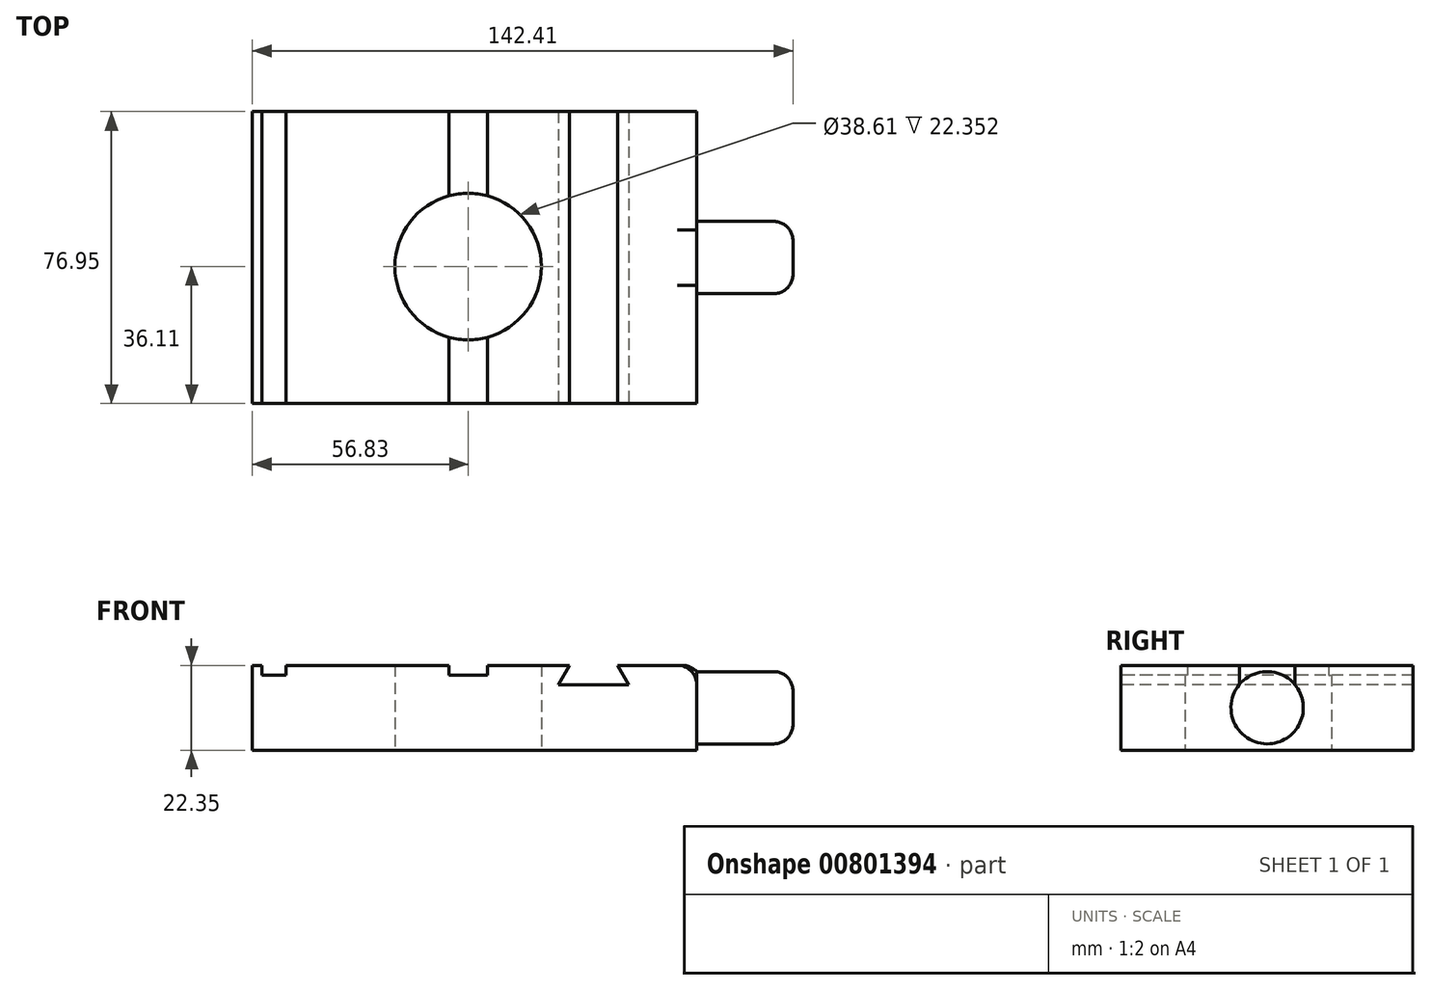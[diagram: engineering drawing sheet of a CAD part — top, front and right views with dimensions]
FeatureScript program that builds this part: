
annotation { "Feature Type Name" : "Feature", "Feature Type Description" : "" }
export const myFeature = defineFeature(function(context is Context, id is Id, definition is map)
    precondition{}
    {
        {
            var Q0;
            Q0=qCreatedBy(makeId("Top.planeOp"),FACE);
            var sketch = newSketch(context, id + "F0", { "sketchPlane" : qUnion([Q0])});
            skLineSegment(sketch, "E0.bottom", {"start": v(-56.83, 40.84) * mm, "end": v(60.18, 40.84) * mm});
            skLineSegment(sketch, "E0.top", {"start": v(-56.83, -36.1) * mm, "end": v(60.18, -36.1) * mm});
            skLineSegment(sketch, "E0.left", {"start": v(-56.83, 40.84) * mm, "end": v(-56.83, -36.1) * mm});
            skLineSegment(sketch, "E0.right", {"start": v(60.18, 40.84) * mm, "end": v(60.18, -36.1) * mm});
            skCircle(sketch, "E1", {"center": v(0, 0) * mm, "radius": 19.3 * mm});
            skSolve(sketch);
        }
        {
            var Q0;
            Q0 = qSketchRegion(id + "F0", true);
            extrude(context, id + "F1", {"entities" : qUnion([Q0]), "depth" : 22.35 * mm, "offsetDistance" : 25.4 * mm});
        }
        {
            var Q0;
            Q0=makeQuery(id+"F1.opExtrude","CAP_FACE",FACE,{"disambiguationData":[OSD([sQuery(id+"F0.wireOp",EDGE,"E0.bottom"),sQuery(id+"F0.wireOp",EDGE,"E0.top"),sQuery(id+"F0.wireOp",EDGE,"E0.left"),sQuery(id+"F0.wireOp",EDGE,"E0.right"),sQuery(id+"F0.wireOp",EDGE,"E1")])],"isStart":false});
            var sketch = newSketch(context, id + "F2", { "sketchPlane" : qUnion([Q0])});
            skLineSegment(sketch, "E2.bottom", {"start": v(-54.29, 40.84) * mm, "end": v(-47.94, 40.84) * mm});
            skLineSegment(sketch, "E2.top", {"start": v(-54.29, -36.1) * mm, "end": v(-47.94, -36.1) * mm});
            skLineSegment(sketch, "E2.left", {"start": v(-54.29, 40.84) * mm, "end": v(-54.29, -36.1) * mm});
            skLineSegment(sketch, "E2.right", {"start": v(-47.94, 40.84) * mm, "end": v(-47.94, -36.1) * mm});
            skLineSegment(sketch, "E3", {"start": v(-5.08, 40.84) * mm, "end": v(-5.08, -36.1) * mm});
            skLineSegment(sketch, "E4", {"start": v(5.08, 40.84) * mm, "end": v(5.08, -36.1) * mm});
            skSolve(sketch);
        }
        {
            var Q0;
            Q0=makeQuery(id+"F2.imprint","IMPRINT",FACE,{"disambiguationData":[TD([[makeQuery(id+"F2.imprint","IMPRINT",EDGE,{"derivedFrom":sQuery(id+"F2.wireOp",EDGE,"E2.bottom")}),-1.0]])]});
            var Q1;
            {var subQ0=sQuery(id+"F2.wireOp",EDGE,"E3");var subQ1=makeQuery(id+"F1.opExtrude","CAP_EDGE",EDGE,{"disambiguationData":[OSD([sQuery(id+"F0.wireOp",EDGE,"E0.top")])],"isStart":false});var subQ2=makeQuery(id+"F2.imprint","INTERSECT",VERTEX,{"derivedFrom":[subQ1,subQ0]});Q1=makeQuery(id+"F2.imprint","IMPRINT",FACE,{"disambiguationData":[TD([[makeQuery(id+"F2.imprint","IMPRINT",EDGE,{"disambiguationData":[TD([[subQ2,1.0]])],"derivedFrom":subQ0}),1.0]])]});}
            var Q2;
            {var subQ0=sQuery(id+"F2.wireOp",EDGE,"E3");var subQ1=makeQuery(id+"F1.opExtrude","CAP_EDGE",EDGE,{"disambiguationData":[OSD([sQuery(id+"F0.wireOp",EDGE,"E1")])],"isStart":false});var subQ2=makeQuery(id+"F2.imprint","INTERSECT",VERTEX,{"disambiguationData":[OD(0.0)],"derivedFrom":[subQ1,subQ0]});Q2=makeQuery(id+"F2.imprint","IMPRINT",FACE,{"disambiguationData":[TD([[makeQuery(id+"F2.imprint","IMPRINT",EDGE,{"disambiguationData":[TD([[subQ2,-1.0]])],"derivedFrom":subQ0}),1.0]])]});}
            var Q3;
            {var subQ0=sQuery(id+"F2.wireOp",EDGE,"E3");var subQ1=makeQuery(id+"F1.opExtrude","CAP_EDGE",EDGE,{"disambiguationData":[OSD([sQuery(id+"F0.wireOp",EDGE,"E0.bottom")])],"isStart":false});var subQ2=makeQuery(id+"F2.imprint","INTERSECT",VERTEX,{"derivedFrom":[subQ1,subQ0]});Q3=makeQuery(id+"F2.imprint","IMPRINT",FACE,{"disambiguationData":[TD([[makeQuery(id+"F2.imprint","IMPRINT",EDGE,{"disambiguationData":[TD([[subQ2,-1.0]])],"derivedFrom":subQ0}),1.0]])]});}
            extrude(context, id + "F3", {"entities" : qUnion([Q0, Q1, Q2, Q3]), "operationType" : NewBodyOperationType.REMOVE, "oppositeDirection" : true, "depth" : 2.54 * mm, "offsetDistance" : 25.4 * mm});
        }
        {
            var Q0;
            Q0=makeQuery(id+"F1.opExtrude","SWEPT_FACE",FACE,{"disambiguationData":[OSD([sQuery(id+"F0.wireOp",EDGE,"E0.top")])]});
            var sketch = newSketch(context, id + "F4", { "sketchPlane" : qUnion([Q0])});
            skLineSegment(sketch, "E5", {"start": v(26.67, 22.35) * mm, "end": v(23.74, 17.27) * mm});
            skLineSegment(sketch, "E6", {"start": v(23.74, 17.27) * mm, "end": v(42.3, 17.27) * mm});
            skLineSegment(sketch, "E7", {"start": v(42.3, 17.27) * mm, "end": v(39.37, 22.35) * mm});
            skLineSegment(sketch, "E8", {"start": v(39.37, 22.35) * mm, "end": v(26.67, 22.35) * mm});
            skLineSegment(sketch, "E9", {"start": v(33.02, 17.27) * mm, "end": v(33.02, 22.35) * mm, "construction": true});
            skSolve(sketch);
        }
        {
            var Q0;
            Q0=makeQuery(id+"F4.imprint","IMPRINT",FACE,{"disambiguationData":[TD([[makeQuery(id+"F4.imprint","IMPRINT",EDGE,{"derivedFrom":sQuery(id+"F4.wireOp",EDGE,"E5")}),1.0]])]});
            extrude(context, id + "F5", {"entities" : qUnion([Q0]), "operationType" : NewBodyOperationType.REMOVE, "endBound" : BoundingType.THROUGH_ALL, "oppositeDirection" : true, "depth" : 31.24 * mm, "offsetDistance" : 25.4 * mm});
        }
        {
            var Q0;
            Q0=makeQuery(id+"F1.opExtrude","SWEPT_FACE",FACE,{"disambiguationData":[OSD([sQuery(id+"F0.wireOp",EDGE,"E0.right")])]});
            var sketch = newSketch(context, id + "F6", { "sketchPlane" : qUnion([Q0])});
            skCircle(sketch, "E10", {"center": v(2.37, 11.18) * mm, "radius": 9.53 * mm});
            skPoint(sketch, "E10.centerSnap0", {"position": v(-36.1, 11.18) * mm});
            skPoint(sketch, "E10.centerSnap1", {"position": v(2.37, 22.35) * mm});
            skSolve(sketch);
        }
        {
            var Q0;
            Q0=makeQuery(id+"F6.imprint","IMPRINT",FACE,{"disambiguationData":[TD([[makeQuery(id+"F6.imprint","IMPRINT",EDGE,{"derivedFrom":sQuery(id+"F6.wireOp",EDGE,"E10")}),1.0]])]});
            extrude(context, id + "F7", {"entities" : qUnion([Q0]), "operationType" : NewBodyOperationType.ADD, "depth" : 25.4 * mm, "offsetDistance" : 25.4 * mm});
        }
        {
            var Q0;
            Q0=makeQuery(id+"F1.opExtrude","CAP_EDGE",EDGE,{"disambiguationData":[OSD([sQuery(id+"F0.wireOp",EDGE,"E0.right")])],"isStart":false});
            var Q1;
            Q1=makeQuery(id+"F7.opExtrude","CAP_EDGE",EDGE,{"disambiguationData":[OSD([sQuery(id+"F6.wireOp",EDGE,"E10")])],"isStart":false});
            fillet(context, id + "F8", {"entities" : qUnion([Q0, Q1]), "radius" : 5.08 * mm, "tangentPropagation" : true, "allowEdgeOverflow" : false});
        }
    });
